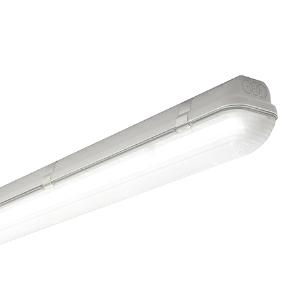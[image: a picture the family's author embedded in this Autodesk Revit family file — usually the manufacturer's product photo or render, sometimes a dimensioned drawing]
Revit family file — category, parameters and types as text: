
# Revit family: 3f_filippi_-_3f_linda_soft_3f_filippi_-_58735_-_3f_linda_led_soft_1x24w_dali_l1270
name_source: partatom
category: Lighting Fixtures
units: mm (PartAtom-declared; Revit-internal decimal feet)

## family parameters
Cut with Voids When Loaded = No
Host = Face
Light Source = No
Part Type = Normal
Room Calculation Point = No
Round Connector Dimension = Use Diameter
Shared = No

## types (1)
- 3F Filippi - 3F Linda Soft (1 x LED, 3732 lm, 28 W, 4000 K)
    Apparent Load = 28 VA
    Approval mark = CE
    CIE Flux Codes = 39 68 88 89 100
    Color Rendering = 80
    Color Temperature = 4000 K
    Control Gear = Electronic transformer
    Default Elevation = 1800 mm
    Description = ILLUMINOTECHNICAL
Luminous efficiency 100% (DLOR 89%, ULOR 11%).
Initial luminous flux of the luminaire 3732 lm.
Direct symmetric distribution.
Installation Interdistance Transv.D = 1.39 x hu - Long.D = 1.21 x hu.
Tabular UGR (CIE 117 - 4H-8H; S=0.25H; 70/50/20): RUG 23.9 - 20.8.
Beam angle: 149° - 108°.
Luminous efficacy 133 lm/W.
Lifetime (L93/B10): 30000 h. (tq+25°C)
Lifetime (L90/B10): 50000 h. (tq+25°C)
Lifetime (L85/B10): 80000 h. (tq+25°C)
Lifetime (L80/B10): 100000 h. (tq+25°C)
Lifetime (L85/B10): 50000 h. (tq+35°C)
Sudden decreased luminous flux after 50000 hours: 0% (C0).
Photobiological safety in compliance with IEC/TR 62778: RG0 risk exempt, (IEC 62471).
In compliance with IEC/EN 62722-2-1 - IEC/EN 62717 standards.

SOURCE
Linear LED module 24W/840.
Energy efficiency class (UE 2019/2020 - UE 2019/2015): D.
CIE 13.3 Colour rendering index: CRI >80 (R9 <50%).
IES TM-30 Fidelity Index: Rf = 84 Rg = 95.
CCT nominal colour temperature 4000 K.
Colour initial tolerance (MacAdam): SDCM 3.

MECHANICAL
Self-extinguishing V2 polycarbonate housing, injection moulded, RAL 7035 grey.
Ecologic anti-aging injected sealing gasket.
Soft opal diffuser in self-extinguishing V2 polycarbonate, photo-engraved interior, UV stabilised, injection moulded.
Gear-holder reflector in hot-dip galvanised steel, painted with white polyester base.
Snug fit safety snap-lock clips for diffuser mounting in stainless steel, screwdriver opening.
Fixing brackets in stainless steel.
Possibility for technicians to access the interior of the luminaire.
Luminaire with limited surface temperature. - D - (EN 60598-2-24)
Dimensions: 1270x100 mm, height 100 mm. Weight 2.03 kg.
IP66 protection degree.
Mechanical strength to impacts IK10 (20 joule).
Glow-wire test resistance 850°C.

ELECTRICAL
Halogen Free DALI-2 DATI (Parts 251, 252, 253), PUSH-DIM, electronic wiring 230V-50/60Hz, power factor 0.90 at full load, THD <25%, constant output current, SELV, class I, 1 driver, 1 DALI addresse.
Power of the luminaire 28 W.
ENEC - CE.
SAFE FLICKER: PstLM=<1 and SVM=<0.4 (IEC TR 61547-1 and IEC TR 63158), to ensure a more comfortable and safe light.
Luminaire compliant with EN 60598-2-22 for power supply from a centralised emergency system CPSS (Central Power Supply System), not incorporated in the luminaire - high risk areas excluded. The default power and flux are 100% in AC and 15% in DC.
Ambient temperature from -20°C to +35°C.
Temperature class T6 max 85°C.
Relative humidity UR: <85%.

INSTALLATION
Ceiling / Suspended / Wall.
All accessories dedicated to this product are available on the Catalog and on our website www.3F-Filippi.com.

APPLICATIONS
Suitable product for food production plants (HACCP), IFS (Food Version 6), BRC (GSFS Food Version 7).
Dry, dusty indoor environments, subject to occasional water splashes.
Luminaires designed for diffuse direct/indirect lighting suitable to provide optimum visual comfort.
Transit areas, stairwells.
Virtually shatterproof polycarbonate compatibly with the fumes / atmospheres that compromise the elasticity of plastic materials.
Suitable for illumination of public car parks and parking grounds referred to DIN 67528:2018-04.

LIGHT MANAGEMENT
Recommended minimum setting: 10%.
The luminaire, equipped with (DALI-2 DATI) driver, can be controlled manually with 3F Easy Dim technology or automatically/manually with wired or wireless DALI/D2D control systems.
The D2D driver guarantees interoperability with other devices with the same certification by making the following information available:
Device Data (Part 251), Energy Report (Part 252), Diagnosis & Maintenance (Part 253).
In electrical systems without a regulation system (manual or automatic) and DALI bus, a suitable jumper must be made on the DA-DA terminals of the appliance.

WARNING
Fixture not suitable for cold stores with an ambient temperature <0°C and/or relative humidity >85%.
Luminaire designed for disposal/recycling at end-of-life.
Replaceable (LED only) light source by a professional. Replaceable control gear by a professional.
    Height = 100 mm  [stored 0.328084 ft]
    Lamp = 1 x LED
    Lamp Light Flux = 3732 lm
    Lamp Power = 28 W
    Lamp count = 1
    Length = 1270 mm
    Lifetime = 50000 h
    Luminous efficacy = 133 lm/W
    Manufacturer = 3F Filippi
    ModVariant = No
    Model = 3F Filippi - 58735 - 3F Linda LED Soft 1x24W DALI L1270
    Mounting Place = Ceiling
    Mounting Type = Pendant
    Number of Poles = 1
    OnlyDefault = Yes
    Power Factor = 1
    Product Name = 3F Filippi - 3F Linda Soft
    Product group = pendant luminaire
    ProductGroupID = 9
    Protection Class = Protection class I
    Protection Degree = IP 66
    RLX_Detail_Level = 1
    RLX_Emergency_Light_Flux = 0 lm
    RLX_Emergency_Type = 0
    RLX_Emergency_Type_DB = No
    RlxData = <blob elided: 62705 chars, md5=a8801dbc>
    Socket = socket
    Standby Power = 0 W
    System Light Flux = 3732 lm
    System Power = 28 W
    Type Comments = Product without accessories
    Type Image = 3ffilippi_3f_linda_led_soft_1x.jpg
    URL = http://relux.com
    VarID = ---
    Voltage = 0 V
    Weight = 0.00 kg
    Width = 100 mm  [stored 0.328084 ft]

note: [stored X ft] marks values corroborated as IEEE doubles in the binary element streams (Revit-internal decimal feet)

## geometry (parser evidence)
native form markers: Blend x4, Sweep x13
no freeform markers — native parametric forms only
